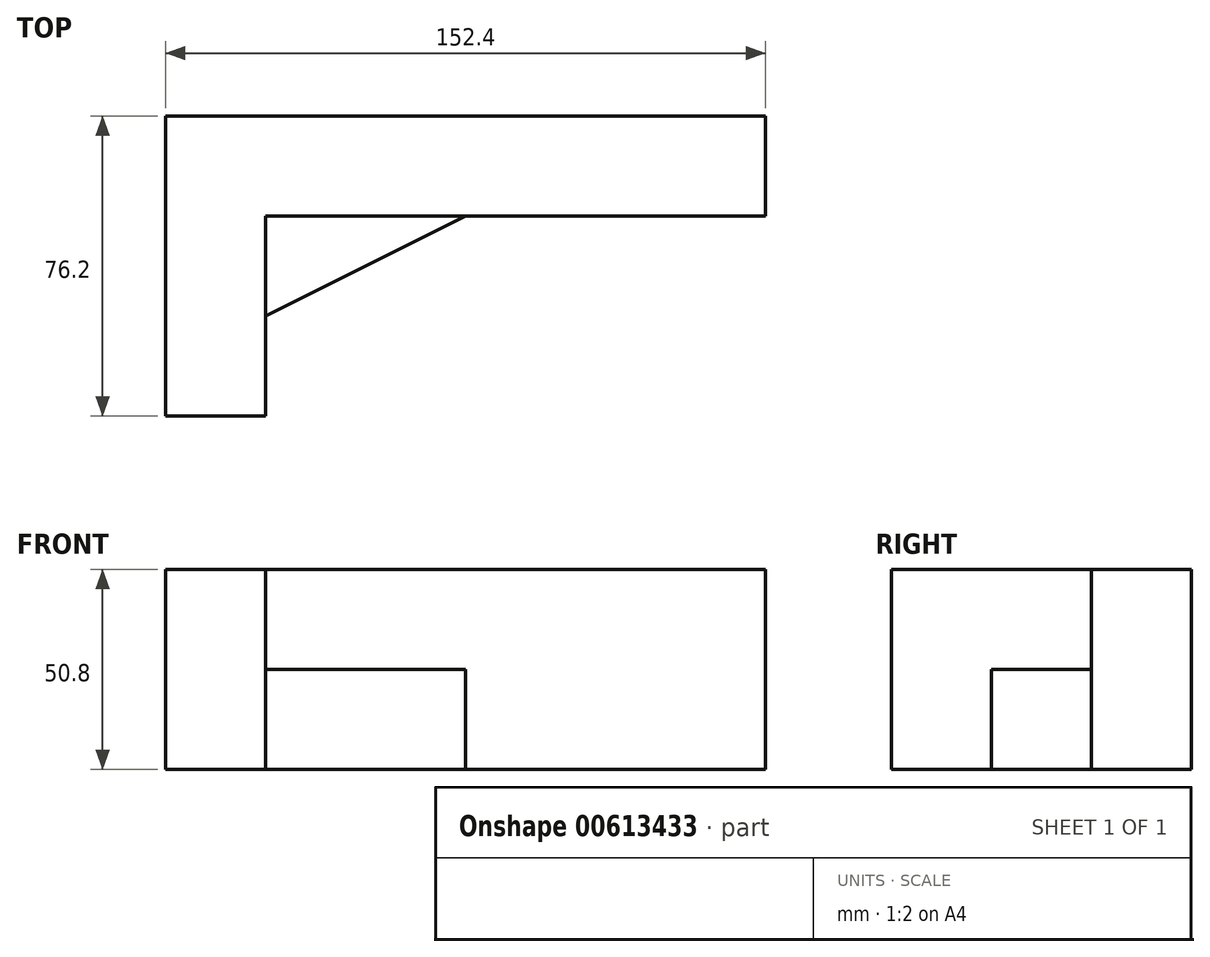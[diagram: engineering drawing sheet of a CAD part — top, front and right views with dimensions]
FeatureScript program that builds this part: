
annotation { "Feature Type Name" : "Feature", "Feature Type Description" : "" }
export const myFeature = defineFeature(function(context is Context, id is Id, definition is map)
    precondition{}
    {
        {
            var Q0;
            Q0=qCreatedBy(makeId("Top.planeOp"),FACE);
            var sketch = newSketch(context, id + "F0", { "sketchPlane" : qUnion([Q0])});
            skLineSegment(sketch, "E0", {"start": v(0, 0) * mm, "end": v(25.4, 0) * mm});
            skLineSegment(sketch, "E1", {"start": v(25.4, 0) * mm, "end": v(25.4, 50.8) * mm});
            skLineSegment(sketch, "E2", {"start": v(25.4, 50.8) * mm, "end": v(152.4, 50.8) * mm});
            skLineSegment(sketch, "E3", {"start": v(152.4, 50.8) * mm, "end": v(152.4, 76.2) * mm});
            skLineSegment(sketch, "E4", {"start": v(152.4, 76.2) * mm, "end": v(0, 76.2) * mm});
            skLineSegment(sketch, "E5", {"start": v(0, 76.2) * mm, "end": v(0, 0) * mm});
            skSolve(sketch);
        }
        {
            var Q0;
            Q0 = qSketchRegion(id + "F0", true);
            extrude(context, id + "F1", {"entities" : qUnion([Q0]), "depth" : 50.8 * mm, "offsetDistance" : 25.4 * mm});
        }
        {
            var Q0;
            Q0=makeQuery(id+"F1.opExtrude","CAP_FACE",FACE,{"disambiguationData":[OSD([sQuery(id+"F0.wireOp",EDGE,"E0"),sQuery(id+"F0.wireOp",EDGE,"E1"),sQuery(id+"F0.wireOp",EDGE,"E2"),sQuery(id+"F0.wireOp",EDGE,"E3"),sQuery(id+"F0.wireOp",EDGE,"E4"),sQuery(id+"F0.wireOp",EDGE,"E5")])],"isStart":true});
            var sketch = newSketch(context, id + "F2", { "sketchPlane" : qUnion([Q0])});
            skLineSegment(sketch, "E6", {"start": v(25.4, -50.8) * mm, "end": v(76.2, -50.8) * mm});
            skLineSegment(sketch, "E7", {"start": v(76.2, -50.8) * mm, "end": v(25.4, -25.4) * mm});
            skLineSegment(sketch, "E8", {"start": v(25.4, -25.4) * mm, "end": v(25.4, -50.8) * mm});
            skSolve(sketch);
        }
        {
            var Q0;
            Q0 = qSketchRegion(id + "F2", true);
            extrude(context, id + "F3", {"entities" : qUnion([Q0]), "oppositeDirection" : true, "depth" : 25.4 * mm, "offsetDistance" : 25.4 * mm});
        }
    });
